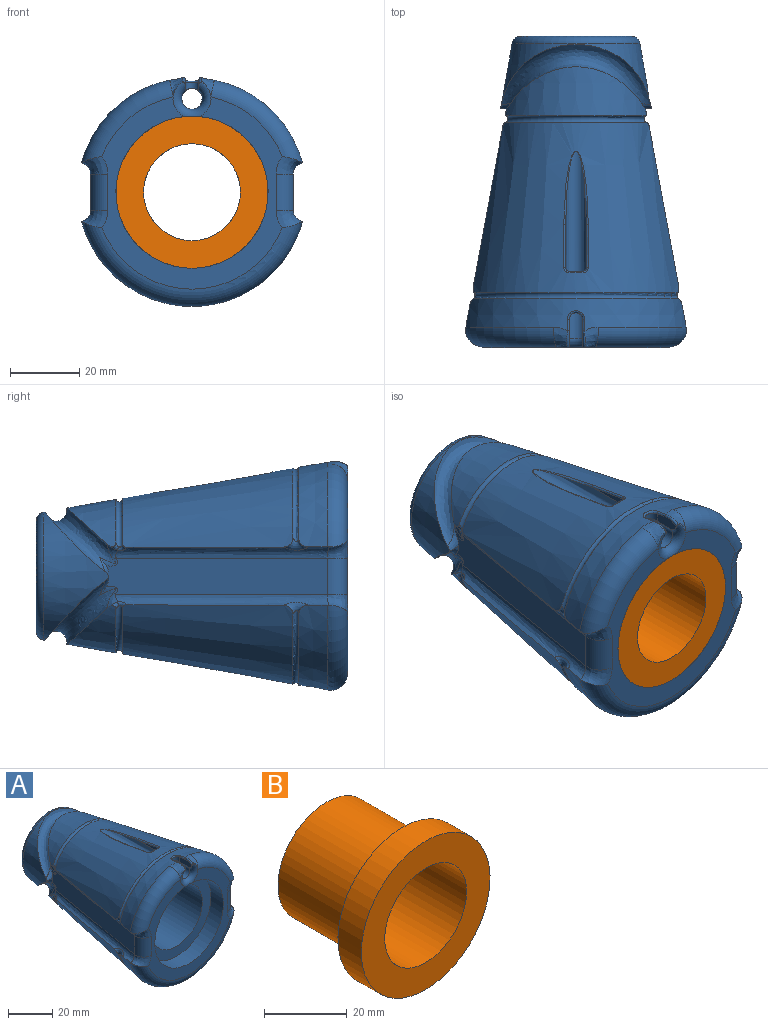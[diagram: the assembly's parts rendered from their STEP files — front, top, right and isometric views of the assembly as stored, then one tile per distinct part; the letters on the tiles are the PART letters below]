
ASSEMBLY  parts=2 mates=1
PART A: 86 faces, bbox 74.1x94.1x71.2 mm
  f0: cone r=34mm half-angle=10deg, axis (0,-1,0), area 502.9mm2, adj f35,f40,f42,f72,f83,f85
  f1: cone r=34mm half-angle=10deg, axis (0,-1,0), area 502.9mm2, adj f9,f26,f28,f73,f79,f81
  f2: cone r=34mm half-angle=10deg, axis (0,-1,0), area 3133.6mm2, adj f36,f37,f64,f65,f66,f67,f68,f69
  f3: cone r=34mm half-angle=10deg, axis (0,-1,0), area 3352.3mm2, adj f20,f21,f71,f73,f74,f75,f78,f80
  f4: plane 0.63x0.43mm, normal (0,1,0), area 0.1mm2, adj f5,f60,f69
  f5: cylinder r=3mm len=54.19mm, axis (0,-1,0), area 591.6mm2, adj f4,f7,f51,f52,f53,f59,f60,f61
  f6: cone r=34mm half-angle=10deg, axis (0,-1,0), area 676.2mm2, adj f8,f36,f37,f45,f46,f47,f55,f56
  f7: torus R=5.5mm, axis (0,-1,0), area 78.6mm2, adj f5,f8,f11,f16,f46,f51,f52,f54
  f8: bspline ~5.87x5.84mm, area 23.1mm2, adj f6,f7,f47,f58
  f9: bspline ~56.83x28.03mm, area 575.5mm2, adj f1,f10,f24,f25,f26,f27,f28,f29
  f10: cone r=34mm half-angle=10deg, axis (0,-1,0), area 791.6mm2, adj f9,f24,f25,f35,f38,f39,f49
  f11: plane 55.54x52.17mm, normal (0,-1,0), area 779.5mm2, adj f7,f16,f30,f31,f32,f33,f34,f44
  f12: cone r=34mm half-angle=10deg, axis (0,-1,0), area 693.6mm2, adj f20,f21,f32,f71,f74,f75
  f13: plane 33x33mm, normal (0,-1,0), area 239.5mm2, adj f14,f17
  f14: cylinder r=16.5mm len=33mm, axis (0,-1,0), area 2695.5mm2, adj f13,f15
  f15: plane 44x44mm, normal (0,-1,0), area 665.2mm2, adj f14,f16
  f16: cylinder r=22mm len=44mm, axis (0,-1,0), area 1105.8mm2, adj f7,f11,f15
  f17: cylinder r=14mm len=51.98mm, axis (0,-1,0), area 4572mm2, adj f13,f50
  f18: plane 64.25x11.51mm, normal (0.99,0.17,0), area 662.7mm2, adj f19,f20,f25,f29,f30,f36,f39,f43
  f19: plane 0.87x0.71mm, normal (0,-1,0), area 0.3mm2, adj f18,f25,f39
  f20: bspline ~69x18.68mm, area 244.8mm2, adj f3,f12,f18,f28,f31,f32,f74,f80
  f21: bspline ~69x18.68mm, area 244.8mm2, adj f3,f12,f23,f26,f32,f33,f75,f78
  f22: plane 0.86x0.71mm, normal (0,-1,0), area 0.3mm2, adj f23,f24,f38
  f23: plane 64.25x11.51mm, normal (-0.99,0.17,0), area 662.6mm2, adj f21,f22,f24,f27,f34,f37,f38,f41
  f24: bspline ~8.03x6.68mm, area 12.3mm2, adj f9,f10,f22,f23,f27,f38
  f25: bspline ~7.3x6.56mm, area 12.4mm2, adj f9,f10,f18,f19,f29,f39
  f26: bspline ~4.71x3.32mm, area 9.5mm2, adj f1,f9,f21,f27,f79
  f27: bspline ~6.07x3.45mm, area 5.9mm2, adj f9,f23,f24,f26
  f28: bspline ~4.74x3.34mm, area 9.5mm2, adj f1,f9,f20,f29,f81
  f29: bspline ~6.28x2.94mm, area 5.9mm2, adj f9,f18,f25,f28
  f30: cylinder r=5mm len=10.48mm, axis (0,0,-1), area 91.4mm2, adj f11,f18,f31,f44
  f31: bspline ~9.9x7.81mm, area 40.2mm2, adj f11,f20,f30,f32
  f32: torus R=28.04mm, axis (0,-1,0), area 697.4mm2, adj f11,f12,f20,f21,f31,f33
  f33: bspline ~9.9x7.81mm, area 40.2mm2, adj f11,f21,f32,f34
  f34: cylinder r=5mm len=10.48mm, axis (0,0,1), area 91.4mm2, adj f11,f23,f33,f48
  f35: bspline ~47.5x21.61mm, area 575.5mm2, adj f0,f10,f38,f39,f40,f41,f42,f43
  f36: bspline ~69x18.68mm, area 244.8mm2, adj f2,f6,f18,f42,f44,f45,f76,f84
  f37: bspline ~69x18.68mm, area 244.8mm2, adj f2,f6,f23,f40,f47,f48,f77,f82
  f38: bspline ~8.08x6.84mm, area 12.4mm2, adj f10,f22,f23,f24,f35,f41
  f39: bspline ~7.98x7.5mm, area 12.5mm2, adj f10,f18,f19,f25,f35,f43
  f40: bspline ~4.7x3.32mm, area 9.5mm2, adj f0,f35,f37,f41,f83
  f41: bspline ~6.14x3.46mm, area 5.9mm2, adj f23,f35,f38,f40
  f42: bspline ~4.74x3.34mm, area 9.5mm2, adj f0,f35,f36,f43,f85
  f43: bspline ~6.28x2.94mm, area 5.9mm2, adj f18,f35,f39,f42
  f44: bspline ~9.9x7.81mm, area 40.2mm2, adj f11,f30,f36,f45
  f45: torus R=28.04mm, axis (0,-1,0), area 294.8mm2, adj f6,f11,f36,f44,f46
  f46: bspline ~5.87x5.84mm, area 23.1mm2, adj f6,f7,f45,f54
  f47: torus R=28.04mm, axis (0,-1,0), area 294.8mm2, adj f6,f8,f11,f37,f48
  f48: bspline ~9.9x7.81mm, area 40.2mm2, adj f11,f34,f37,f47
  f49: torus R=16.03mm, axis (0,-1,0), area 384.1mm2, adj f10,f50
  f50: torus R=19mm, axis (0,1,0), area 432mm2, adj f17,f49
  f51: plane 8.12x3.66mm, normal (1,0,0), area 22.8mm2, adj f5,f7,f53,f57,f58
  f52: plane 8.12x3.66mm, normal (-1,0,0), area 22.8mm2, adj f5,f7,f53,f54,f55
  f53: cylinder r=2mm len=4mm, axis (0,0,1), area 17.3mm2, adj f5,f51,f52,f56
  f54: bspline ~7.15x2.58mm, area 4.8mm2, adj f7,f46,f52,f55
  f55: bspline ~16.4x3.41mm, area 2.7mm2, adj f6,f52,f54,f56
  f56: bspline ~5.08x3.07mm, area 5.9mm2, adj f6,f53,f55,f57
  f57: bspline ~16.4x3.41mm, area 2.7mm2, adj f6,f51,f56,f58
  f58: bspline ~7.15x2.58mm, area 4.8mm2, adj f7,f8,f51,f57
  f59: plane 12.54x2.23mm, normal (1,0,0), area 14mm2, adj f5,f60,f65
  f60: cylinder r=1mm len=2.63mm, axis (0,0,1), area 2.1mm2, adj f4,f5,f59,f67
  f61: plane 0.63x0.43mm, normal (0,1,0), area 0.1mm2, adj f5,f62,f69
  f62: cylinder r=1mm len=2.63mm, axis (0,0,1), area 2.1mm2, adj f5,f61,f63,f68
  f63: plane 12.54x2.23mm, normal (-1,0,0), area 14mm2, adj f5,f62,f66
  f64: bspline ~25.81x7.13mm, area 23.8mm2, adj f2,f5,f65,f66
  f65: bspline ~62.79x11.69mm, area 10.8mm2, adj f2,f59,f64,f67
  f66: bspline ~43.99x8.36mm, area 10.8mm2, adj f2,f63,f64,f68
  f67: bspline ~1.86x1.83mm, area 1.5mm2, adj f2,f60,f65,f69
  f68: bspline ~1.86x1.83mm, area 1.5mm2, adj f2,f62,f66,f69
  f69: torus R=29.7mm, axis (0,-1,0), area 2.2mm2, adj f2,f4,f5,f61,f67,f68
  f70: torus R=31.84mm, axis (0,-1,0), area 164.6mm2, adj f2,f6,f76,f77
  f71: torus R=31.84mm, axis (0,-1,0), area 164.6mm2, adj f3,f12,f74,f75
  f72: torus R=22.45mm, axis (0,-1,0), area 149.4mm2, adj f0,f2,f82,f83,f84,f85
  f73: torus R=22.45mm, axis (0,-1,0), area 149.4mm2, adj f1,f3,f78,f79,f80,f81
  f74: bspline ~6.93x3.58mm, area 14.2mm2, adj f3,f12,f20,f71
  f75: bspline ~6.93x3.58mm, area 14.2mm2, adj f3,f12,f21,f71
  f76: bspline ~6.93x3.58mm, area 14.2mm2, adj f2,f6,f36,f70
  f77: bspline ~6.93x3.58mm, area 14.2mm2, adj f2,f6,f37,f70
  f78: bspline ~2.72x1.79mm, area 3.1mm2, adj f3,f21,f73,f79
  f79: bspline ~2.36x2.16mm, area 2.5mm2, adj f1,f26,f73,f78
  f80: bspline ~2.72x1.79mm, area 3.1mm2, adj f3,f20,f73,f81
  f81: bspline ~2.36x2.16mm, area 2.5mm2, adj f1,f28,f73,f80
  f82: bspline ~2.72x1.79mm, area 3.1mm2, adj f2,f37,f72,f83
  f83: bspline ~2.36x2.16mm, area 2.5mm2, adj f0,f40,f72,f82
  f84: bspline ~2.72x1.79mm, area 3.1mm2, adj f2,f36,f72,f85
  f85: bspline ~2.36x2.16mm, area 2.5mm2, adj f0,f42,f72,f84
PART B: 6 faces, bbox 44x34x44 mm
  f0: cylinder r=22mm len=44mm, axis (0,1,0), area 1105.8mm2, adj f2,f3
  f1: cylinder r=14mm len=34mm, axis (0,1,0), area 2990.8mm2, adj f2,f5
  f2: plane 44x44mm, normal (0,-1,0), area 904.8mm2, adj f0,f1
  f3: plane 44x44mm, normal (0,1,0), area 665.2mm2, adj f0,f4
  f4: cylinder r=16.5mm len=33mm, axis (0,-1,0), area 2695.5mm2, adj f3,f5
  f5: plane 33x33mm, normal (0,1,0), area 239.5mm2, adj f1,f4
PLACE A t=(-29.56,-6.77,40.95)mm
PLACE B t=(-29.56,1.23,40.95)mm
MATE cylindrical A.f14 <-> B.f4  axis (0,-1,0) through (-29.56,27.23,40.95)mm
